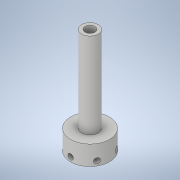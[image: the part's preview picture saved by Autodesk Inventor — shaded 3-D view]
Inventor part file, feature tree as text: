
AUTODESK INVENTOR PART (.ipt)
format: ipt  version: 2022 (Build 260153000, 153)  size: 161,280 bytes
history: native  units: mm
features: extrude x4, sketch x4, pattern_circular x1, projected_geometry x1
ambient origin geometry x8: Origin, YZ Plane, XZ Plane, XY Plane, X Axis, Y Axis, Z Axis, Center Point
bodies: Body1 (feature_tree)
feature tree (10):
  extrude  "Extrusion7"  Depth=5.4mm
  extrude  "Extrusion8"  Depth=5.1mm
  extrude  "Extrusion10"  Depth=20.0mm
  extrude  "Extrusion11"  Depth=10.0mm
  pattern_circular  "Circular Pattern5"  [2 undecoded]
  sketch  "Sketch8"  dims[d57=8.5mm d58=5.4mm]
  sketch  "Sketch9"  dims[d59=4.0mm d60=0.0mm d61=5.1mm]
  projected_geometry  "Projected Loop1"
  sketch  "Sketch11"  dims[d62=50.0mm d63=0.0mm d71=20.0mm]
  sketch  "Sketch12"  dims[d72=10.0mm d73=0.0mm d74=2.8mm d75=0.0mm d76=0.0mm d77=60.0mm d78=360.0deg]
note: 2 required parameter values undecoded (feature->parameter linkage not recoverable at this tier; creation-order binding heuristic only, values carry confidence <= 0.55)
